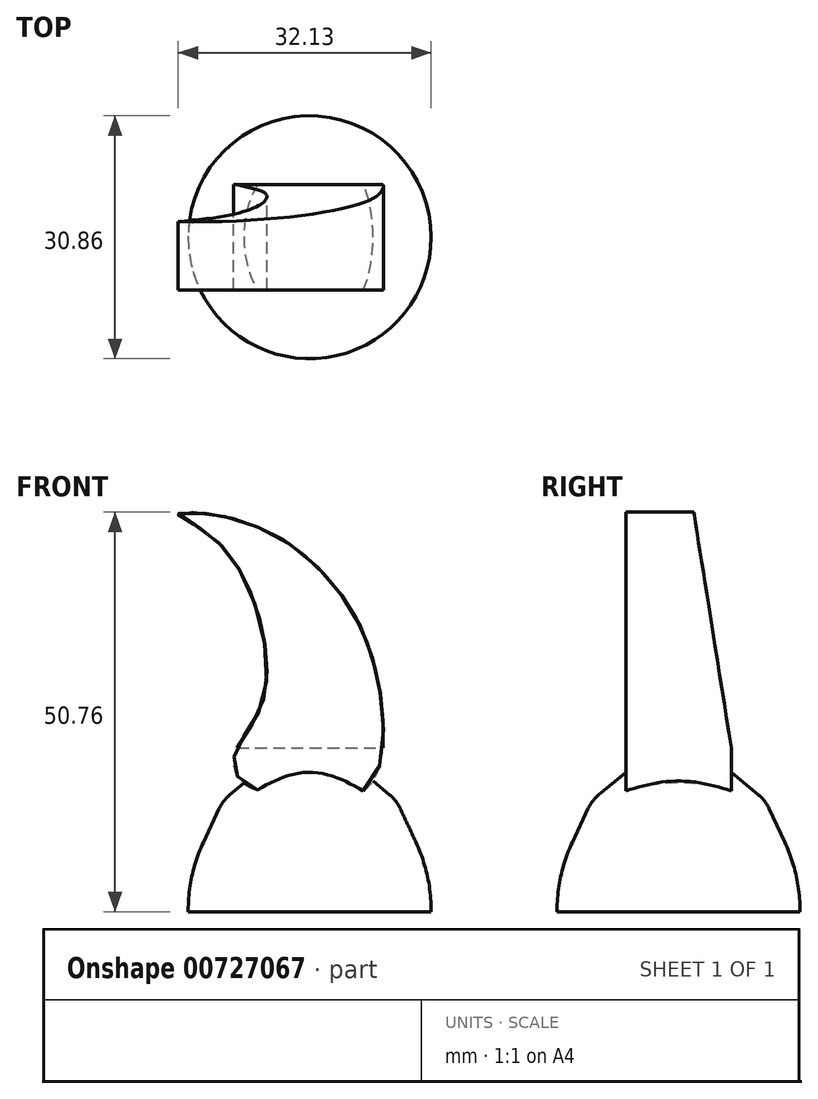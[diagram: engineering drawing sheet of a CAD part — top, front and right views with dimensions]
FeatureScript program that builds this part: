
annotation { "Feature Type Name" : "Feature", "Feature Type Description" : "" }
export const myFeature = defineFeature(function(context is Context, id is Id, definition is map)
    precondition{}
    {
        {
            var Q0;
            Q0=qCreatedBy(makeId("Front.planeOp"),FACE);
            var sketch = newSketch(context, id + "F0", { "sketchPlane" : qUnion([Q0])});
            skLineSegment(sketch, "E0", {"start": v(0, 0) * mm, "end": v(-15.43, 0) * mm});
            skLineSegment(sketch, "E1", {"start": v(-15.43, 0) * mm, "end": v(-15.43, 4.7) * mm});
            skLineSegment(sketch, "E2", {"start": v(-15.43, 4.7) * mm, "end": v(-11.02, 14.13) * mm});
            skLineSegment(sketch, "E3", {"start": v(-11.02, 14.13) * mm, "end": v(-5, 19.14) * mm});
            skLineSegment(sketch, "E4", {"start": v(-5, 19.14) * mm, "end": v(-2.2, 19.94) * mm});
            skLineSegment(sketch, "E5", {"start": v(-2.2, 19.94) * mm, "end": v(0, 19.94) * mm});
            skLineSegment(sketch, "E6", {"start": v(0, 19.94) * mm, "end": v(0, 0) * mm});
            skSolve(sketch);
        }
        {
            var Q0;
            Q0 = qSketchRegion(id + "F0", true);
            var Q1;
            Q1=sQuery(id+"F0.wireOp",EDGE,"E6");
            revolve(context, id + "F1", {"surfaceOperationType" : NewSurfaceOperationType.NEW, "entities" : qUnion([Q0]), "axis" : qUnion([Q1]), "revolveType" : RevolveType.FULL});
        }
        {
            var Q0;
            Q0=makeQuery(id+"F1.opRevolve","SWEPT_FACE",FACE,{"disambiguationData":[OSD([sQuery(id+"F0.wireOp",EDGE,"E3")])]});
            fillet(context, id + "F2", {"entities" : qUnion([Q0]), "radius" : 5 * mm, "tangentPropagation" : true, "allowEdgeOverflow" : false});
        }
        {
            var Q0;
            Q0=makeQuery(id+"F1.opRevolve","SWEPT_FACE",FACE,{"disambiguationData":[OSD([sQuery(id+"F0.wireOp",EDGE,"E2")])]});
            fillet(context, id + "F3", {"entities" : qUnion([Q0]), "radius" : 20.45 * mm, "tangentPropagation" : true, "allowEdgeOverflow" : false});
        }
        {
            var Q0;
            Q0=qCreatedBy(makeId("Front.planeOp"),FACE);
            var sketch = newSketch(context, id + "F4", { "sketchPlane" : qUnion([Q0])});
            skFitSpline(sketch, "E7", {"points": [v(-9.07, 17.07) * mm, v(-2.1, 14.47) * mm, v(7.49, 15.93) * mm, v(9.1, 26.64) * mm, v(6.02, 37.03) * mm, v(-1.93, 46.28) * mm, v(-12.31, 50.5) * mm, v(-16.7, 50.5) * mm, v(-13.13, 48.23) * mm, v(-6.96, 39.14) * mm, v(-5.99, 26.48) * mm, v(-9.23, 20.8) * mm, v(-9.07, 17.07) * mm]});
            skSolve(sketch);
        }
        {
            var Q0;
            Q0=makeQuery(id+"F4.imprint","IMPRINT",FACE,{"disambiguationData":[TD([[makeQuery(id+"F4.imprint","IMPRINT",EDGE,{"derivedFrom":sQuery(id+"F4.wireOp",EDGE,"E7")}),1.0]])]});
            extrude(context, id + "F5", {"entities" : qUnion([Q0]), "operationType" : NewBodyOperationType.ADD, "endBound" : BoundingType.SYMMETRIC, "depth" : 13.4 * mm, "offsetDistance" : 25 * mm});
        }
        {
            var Q0;
            Q0=qCreatedBy(makeId("Right.planeOp"),FACE);
            var sketch = newSketch(context, id + "F6", { "sketchPlane" : qUnion([Q0])});
            skLineSegment(sketch, "E8", {"start": v(1.75, 51.94) * mm, "end": v(7.11, 18.24) * mm});
            skLineSegment(sketch, "E9", {"start": v(7.11, 18.24) * mm, "end": v(15.07, 53.9) * mm});
            skLineSegment(sketch, "E10", {"start": v(15.07, 53.9) * mm, "end": v(1.75, 51.94) * mm});
            skSolve(sketch);
        }
        {
            var Q0;
            Q0 = qSketchRegion(id + "F6", true);
            extrude(context, id + "F7", {"entities" : qUnion([Q0]), "operationType" : NewBodyOperationType.REMOVE, "endBound" : BoundingType.SYMMETRIC, "oppositeDirection" : true, "depth" : 37.6 * mm, "offsetDistance" : 25 * mm});
        }
    });
